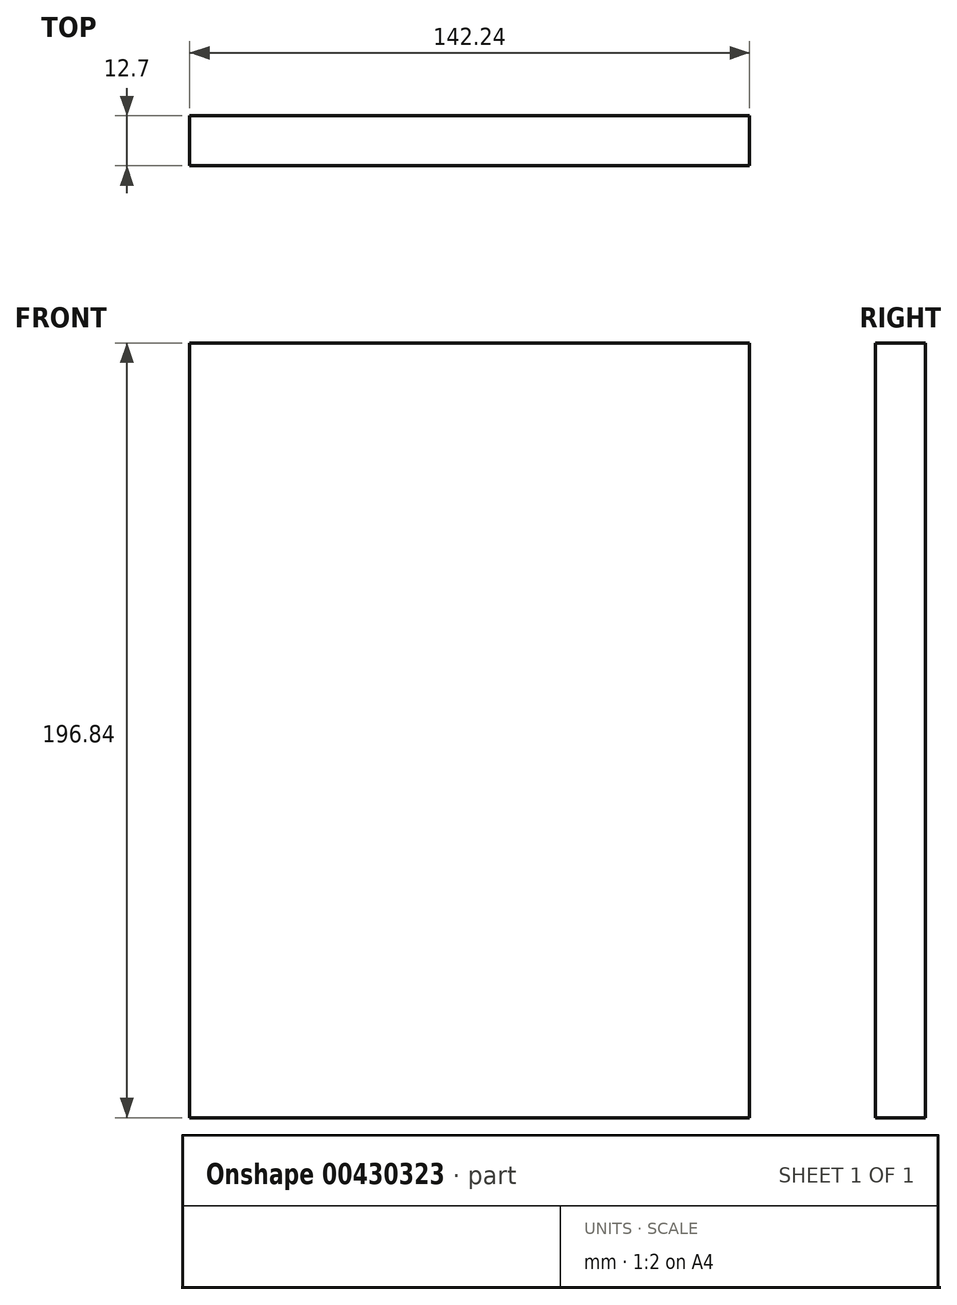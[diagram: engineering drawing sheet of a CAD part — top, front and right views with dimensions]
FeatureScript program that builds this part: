
annotation { "Feature Type Name" : "Feature", "Feature Type Description" : "" }
export const myFeature = defineFeature(function(context is Context, id is Id, definition is map)
    precondition{}
    {
        {
            var Q0;
            Q0=qCreatedBy(makeId("Front.planeOp"),FACE);
            var sketch = newSketch(context, id + "F0", { "sketchPlane" : qUnion([Q0])});
            skLineSegment(sketch, "E0.bottom", {"start": v(71.12, 98.43) * mm, "end": v(-71.12, 98.43) * mm});
            skLineSegment(sketch, "E0.top", {"start": v(71.12, -98.43) * mm, "end": v(-71.12, -98.43) * mm});
            skLineSegment(sketch, "E0.left", {"start": v(71.12, 98.43) * mm, "end": v(71.12, -98.43) * mm});
            skLineSegment(sketch, "E0.right", {"start": v(-71.12, 98.43) * mm, "end": v(-71.12, -98.43) * mm});
            skPoint(sketch, "E0.middle", {"position": v(0, 0) * mm});
            skSolve(sketch);
        }
        {
            var Q0;
            Q0=makeQuery(id+"F0.imprint","IMPRINT",FACE,{"disambiguationData":[TD([[makeQuery(id+"F0.imprint","IMPRINT",EDGE,{"derivedFrom":sQuery(id+"F0.wireOp",EDGE,"E0.bottom")}),1.0]])]});
            extrude(context, id + "F1", {"entities" : qUnion([Q0]), "depth" : 12.7 * mm});
        }
    });
